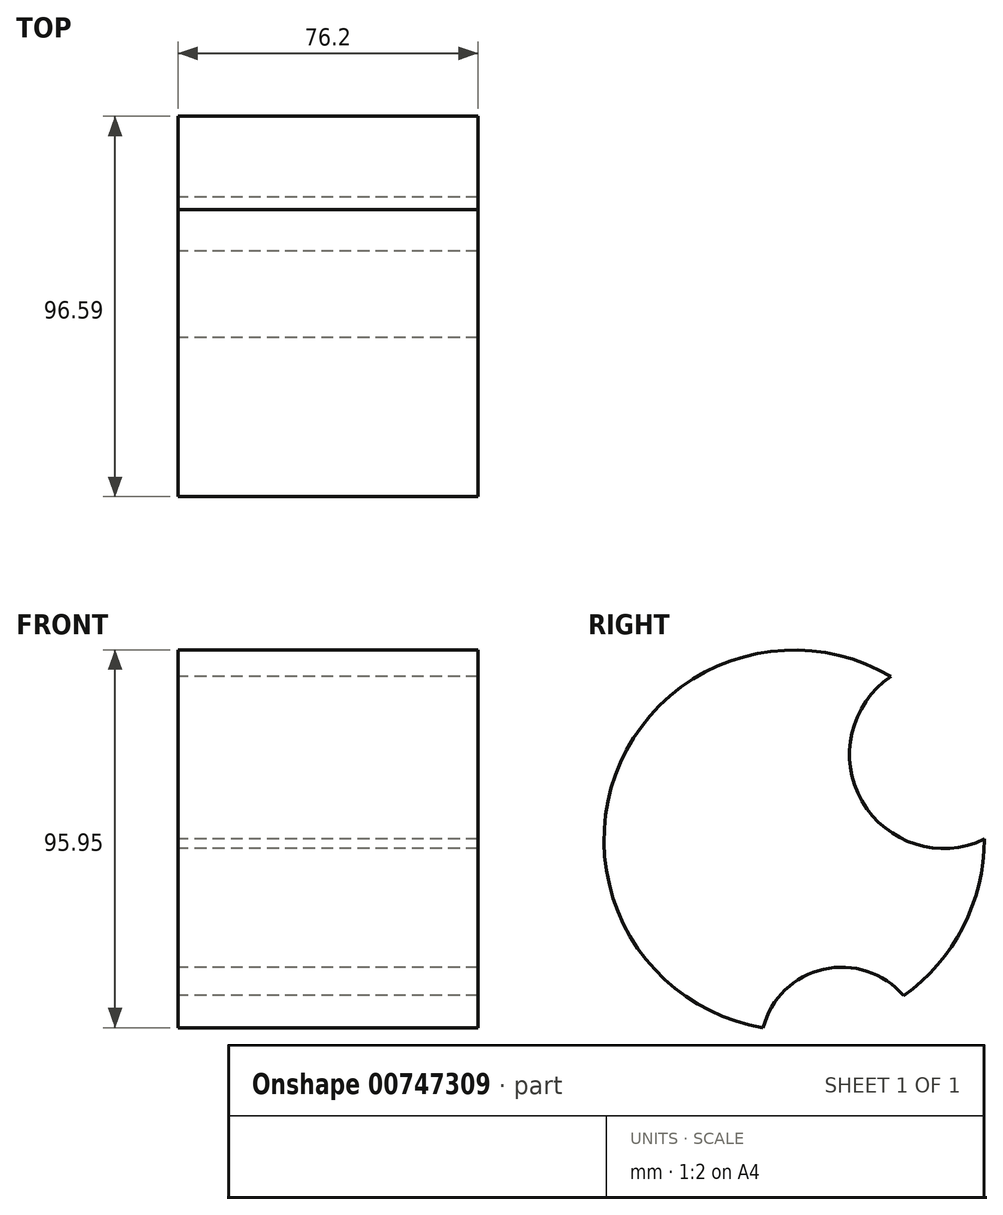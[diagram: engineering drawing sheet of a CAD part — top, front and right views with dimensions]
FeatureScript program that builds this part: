
annotation { "Feature Type Name" : "Feature", "Feature Type Description" : "" }
export const myFeature = defineFeature(function(context is Context, id is Id, definition is map)
    precondition{}
    {
        {
            var Q0;
            Q0=qCreatedBy(makeId("Right.planeOp"),FACE);
            var sketch = newSketch(context, id + "F0", { "sketchPlane" : qUnion([Q0])});
            skCircle(sketch, "E0", {"center": v(-30.93, -31.4) * mm, "radius": 20.64 * mm});
            skCircle(sketch, "E1", {"center": v(-43.02, 21.52) * mm, "radius": 54.3 * mm});
            skCircle(sketch, "E2", {"center": v(-43.02, 21.52) * mm, "radius": 48.3 * mm});
            skCircle(sketch, "E3", {"center": v(-5.05, 43.3) * mm, "radius": 23.87 * mm});
            skSolve(sketch);
        }
        {
            var Q0;
            {var subQ0=sQuery(id+"F0.wireOp",EDGE,"E2");var subQ1=sQuery(id+"F0.wireOp",EDGE,"E0");var subQ2=makeQuery(id+"F0.imprint","INTERSECT",VERTEX,{"disambiguationData":[OD(0.0)],"derivedFrom":[subQ1,subQ0]});Q0=makeQuery(id+"F0.imprint","IMPRINT",FACE,{"disambiguationData":[TD([[makeQuery(id+"F0.imprint","IMPRINT",EDGE,{"disambiguationData":[TD([[subQ2,-1.0]])],"derivedFrom":subQ1}),-1.0]])]});}
            extrude(context, id + "F1", {"entities" : qUnion([Q0]), "depth" : 76.2 * mm, "offsetDistance" : 25.4 * mm});
        }
    });
